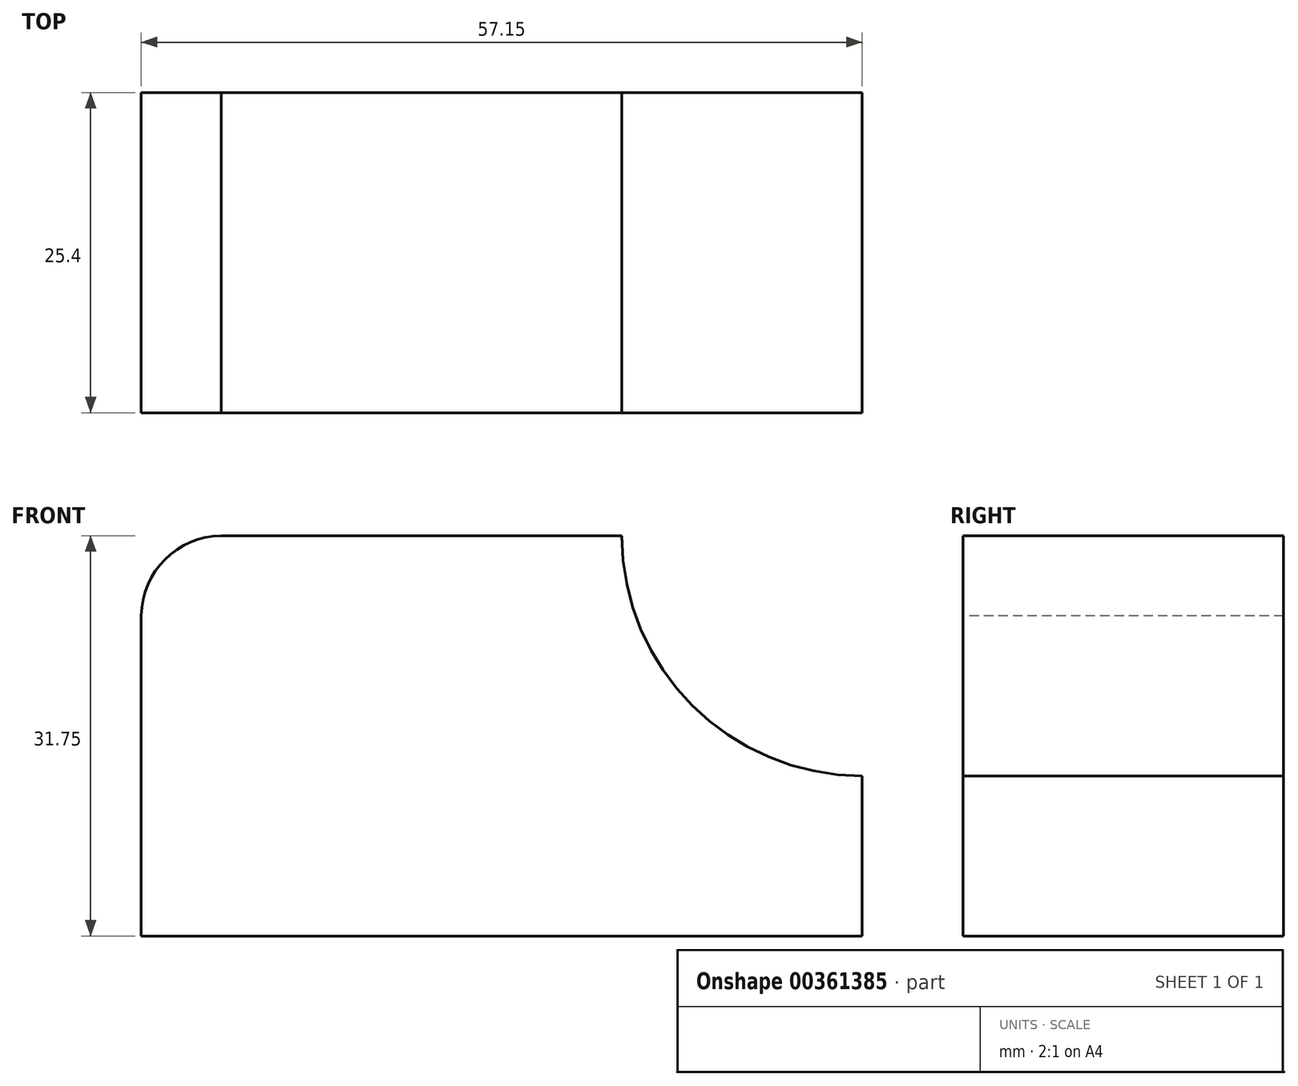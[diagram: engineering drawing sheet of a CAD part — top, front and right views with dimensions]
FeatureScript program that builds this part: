
annotation { "Feature Type Name" : "Feature", "Feature Type Description" : "" }
export const myFeature = defineFeature(function(context is Context, id is Id, definition is map)
    precondition{}
    {
        {
            var Q0;
            Q0=qCreatedBy(makeId("Front.planeOp"),FACE);
            var sketch = newSketch(context, id + "F0", { "sketchPlane" : qUnion([Q0])});
            skLineSegment(sketch, "E0.bottom", {"start": v(-26.13, 22.4) * mm, "end": v(31.02, 22.4) * mm});
            skLineSegment(sketch, "E0.top", {"start": v(-26.13, -9.34) * mm, "end": v(31.02, -9.34) * mm});
            skLineSegment(sketch, "E0.left", {"start": v(-26.13, 22.4) * mm, "end": v(-26.13, -9.34) * mm});
            skLineSegment(sketch, "E0.right", {"start": v(31.02, 22.4) * mm, "end": v(31.02, -9.34) * mm});
            skSolve(sketch);
        }
        {
            var Q0;
            Q0 = qSketchRegion(id + "F0", true);
            extrude(context, id + "F1", {"entities" : qUnion([Q0]), "depth" : 25.4 * mm});
        }
        {
            var Q0;
            Q0=makeQuery(id+"F1.opExtrude","CAP_FACE",FACE,{"disambiguationData":[OSD([sQuery(id+"F0.wireOp",EDGE,"E0.bottom"),sQuery(id+"F0.wireOp",EDGE,"E0.top"),sQuery(id+"F0.wireOp",EDGE,"E0.left"),sQuery(id+"F0.wireOp",EDGE,"E0.right")])],"isStart":false});
            var sketch = newSketch(context, id + "F2", { "sketchPlane" : qUnion([Q0])});
            skLineSegment(sketch, "E1", {"start": v(11.97, 22.4) * mm, "end": v(11.97, 3.36) * mm});
            skLineSegment(sketch, "E2", {"start": v(11.97, 3.36) * mm, "end": v(31.02, 3.36) * mm});
            skArc(sketch, "E3", {"start": v(11.97, 22.4) * mm, "mid": v(17.55, 8.94) * mm, "end": v(31.02, 3.36) * mm});
            skSolve(sketch);
        }
        {
            var Q0;
            {var subQ0=sQuery(id+"F2.wireOp",EDGE,"E3");Q0=makeQuery(id+"F2.imprint","IMPRINT",FACE,{"disambiguationData":[TD([[makeQuery(id+"F2.imprint","IMPRINT",EDGE,{"derivedFrom":subQ0}),1.0]])]});}
            extrude(context, id + "F3", {"entities" : qUnion([Q0]), "operationType" : NewBodyOperationType.REMOVE, "oppositeDirection" : true, "depth" : 25.4 * mm});
        }
        {
            var Q0;
            Q0=makeQuery(id+"F1.opExtrude","CAP_FACE",FACE,{"disambiguationData":[OSD([sQuery(id+"F0.wireOp",EDGE,"E0.bottom"),sQuery(id+"F0.wireOp",EDGE,"E0.top"),sQuery(id+"F0.wireOp",EDGE,"E0.left"),sQuery(id+"F0.wireOp",EDGE,"E0.right")])],"isStart":false});
            var sketch = newSketch(context, id + "F4", { "sketchPlane" : qUnion([Q0])});
            skLineSegment(sketch, "E4", {"start": v(-19.78, 22.4) * mm, "end": v(-19.78, 16.06) * mm});
            skLineSegment(sketch, "E5", {"start": v(-19.78, 16.06) * mm, "end": v(-26.13, 16.06) * mm});
            skArc(sketch, "E6", {"start": v(-19.78, 22.4) * mm, "mid": v(-24.24, 20.53) * mm, "end": v(-26.13, 16.06) * mm});
            skSolve(sketch);
        }
        {
            var Q0;
            {var subQ0=sQuery(id+"F4.wireOp",EDGE,"E6");Q0=makeQuery(id+"F4.imprint","IMPRINT",FACE,{"disambiguationData":[TD([[makeQuery(id+"F4.imprint","IMPRINT",EDGE,{"derivedFrom":subQ0}),-1.0]])]});}
            extrude(context, id + "F5", {"entities" : qUnion([Q0]), "operationType" : NewBodyOperationType.REMOVE, "oppositeDirection" : true, "depth" : 25.4 * mm});
        }
    });
